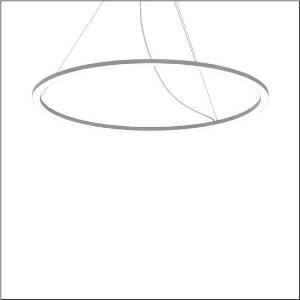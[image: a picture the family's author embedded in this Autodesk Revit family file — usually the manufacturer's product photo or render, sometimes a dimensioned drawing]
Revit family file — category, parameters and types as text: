
# Revit family: silica_r__21_ring-d_5pjbd4d3204a_8650
name_source: partatom
category: Lighting Fixtures
units: mm (PartAtom-declared; Revit-internal decimal feet)

## family parameters
Cut with Voids When Loaded = No
Host = Face
Light Source = No
Part Type = Normal
Room Calculation Point = No
Round Connector Dimension = Use Diameter
Shared = No

## types (1)
- Silica® 21 Ring-D (1 x LED, 11350 lm, 125 W, 4000K)
    Apparent Load = 125 VA
    CIE Flux Codes = 37 69 92 100 100
    Color Rendering = 80
    Color Temperature = 4000K
    Default Elevation = 1800 mm
    Description = Silica® 21 Ring-D, suspended luminaire, of PMMA, frosted, light emission: ring underside luminous distribution, primary light characteristic: symmetric, installation type: suspended mounting, LED, rated luminous flux: 11.350lm, luminous efficacy: 91lm/W, light colour: 840, colour temperature: 4000K, with terminal, 5-pole, mains connection: 230V, AC/DC, 0/50..60Hz, rated input power: 125W, housing, of extruded aluminium section, metallic grey (RAL 9006), diameter: 1.450mm, ceiling canopy, metallic grey (RAL 9006), protection rating (lamp compartment): IP40, insulation class (complete): insulation class I (protective earthing), certification: CE, impact resistance: IK02, permissible operating ambient temperature: 0..+35°C, packaging unit: 1 piece
    Height = 25 mm  [stored 0.082021 ft]
    Lamp = 1 x LED
    Lamp Light Flux = 11350 lm
    Lamp Power = 125 W
    Lamp count = 1
    Length = 1450 mm
    Luminous efficacy = 91 lm/W
    Manufacturer = Siteco
    ModVariant = No
    Model = 5PJBD4D3204A
    Mounting Place = Ceiling
    Mounting Type = Pendant
    Number of Poles = 1
    OnlyDefault = Yes
    Power Factor = 1
    Product Name = Silica® 21 Ring-D
    Product group = suspended luminaire
    ProductGroupID = 904
    Protection Class = Protection class I
    Protection Degree = Degree of protection
    RLX_Detail_Level = 1
    RLX_Emergency_Light_Flux = 0 lm
    RLX_Emergency_Type = 0
    RLX_Emergency_Type_DB = No
    RlxData = <blob elided: 17913 chars, md5=4b3014c4>
    Socket = socket
    Standby Power = 0 W
    System Light Flux = 11350 lm
    System Power = 125 W
    Type Comments = Product without accessories
    Type Image = l_1251748.jpg
    URL = http://relux.com
    VarID = ---
    Voltage = 0 V
    Weight = 0.00 kg
    Width = 0 mm  [stored 0 ft]

note: [stored X ft] marks values corroborated as IEEE doubles in the binary element streams (Revit-internal decimal feet)

## geometry (parser evidence)
native form markers: Blend x4, Sweep x9
no freeform markers — native parametric forms only
